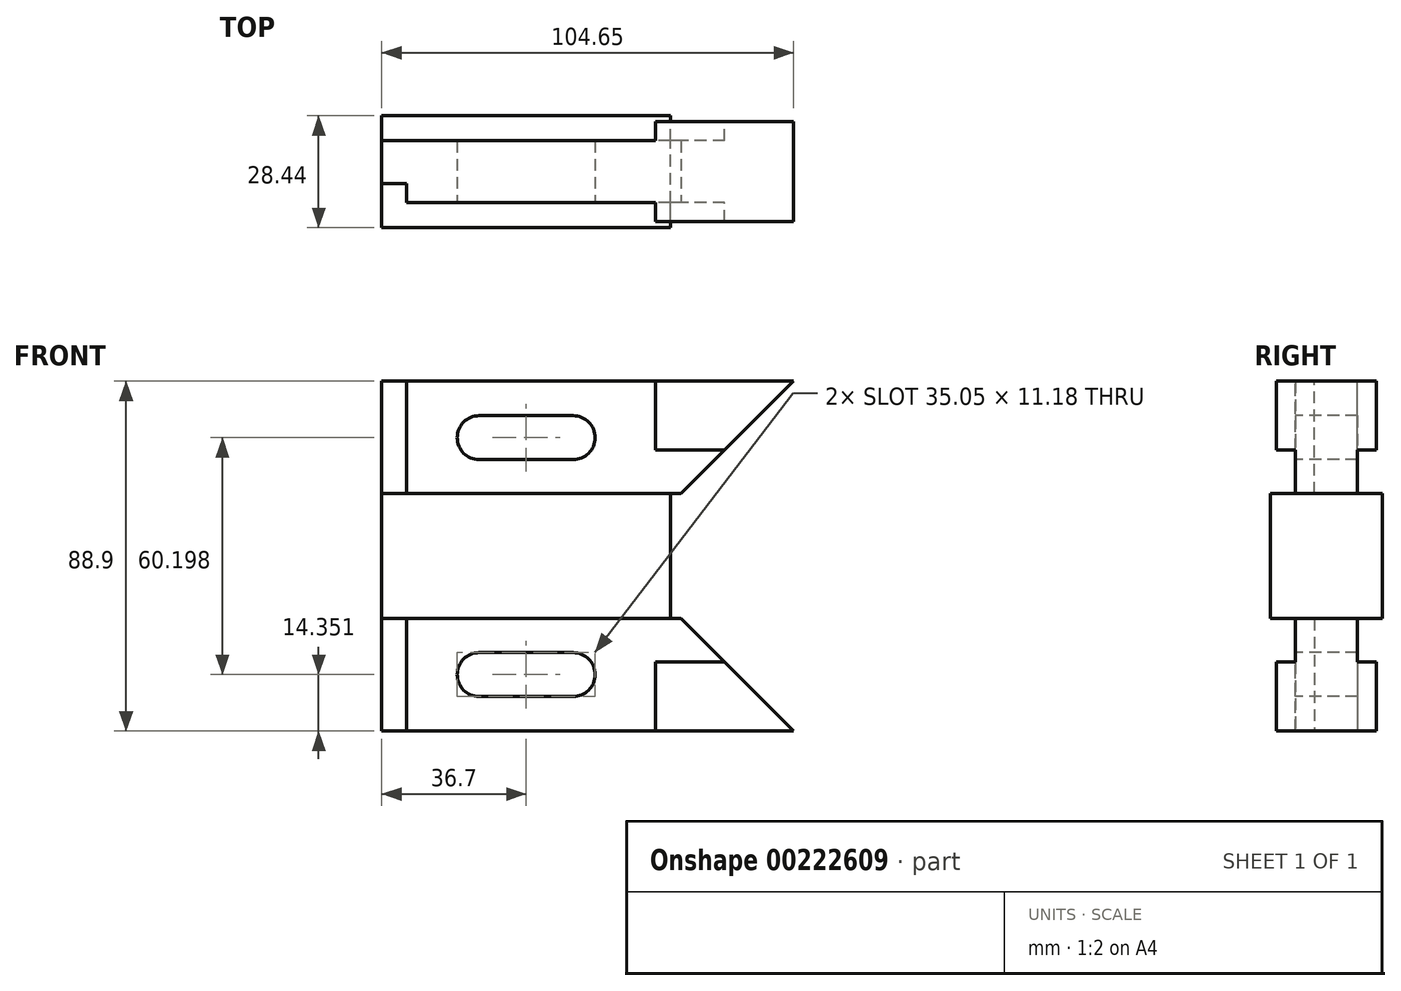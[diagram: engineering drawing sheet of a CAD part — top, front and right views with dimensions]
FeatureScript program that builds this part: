
annotation { "Feature Type Name" : "Feature", "Feature Type Description" : "" }
export const myFeature = defineFeature(function(context is Context, id is Id, definition is map)
    precondition{}
    {
        {
            var Q0;
            Q0=qCreatedBy(makeId("Front.planeOp"),FACE);
            var sketch = newSketch(context, id + "F0", { "sketchPlane" : qUnion([Q0])});
            skLineSegment(sketch, "E0.bottom", {"start": v(36.7, 15.88) * mm, "end": v(-36.7, 15.88) * mm});
            skLineSegment(sketch, "E0.top", {"start": v(36.7, -15.88) * mm, "end": v(-36.7, -15.88) * mm});
            skLineSegment(sketch, "E0.left", {"start": v(36.7, 15.88) * mm, "end": v(36.7, -15.87) * mm});
            skLineSegment(sketch, "E0.right", {"start": v(-36.7, 15.88) * mm, "end": v(-36.7, -15.88) * mm});
            skPoint(sketch, "E0.middle", {"position": v(0, 0) * mm});
            skLineSegment(sketch, "E1", {"start": v(-112.23, 0) * mm, "end": v(159.14, 0) * mm, "construction": true});
            skSolve(sketch);
        }
        {
            var Q0;
            Q0 = qSketchRegion(id + "F0", true);
            extrude(context, id + "F1", {"entities" : qUnion([Q0]), "endBound" : BoundingType.SYMMETRIC, "depth" : 28.45 * mm});
        }
        {
            var Q0;
            Q0=makeQuery(id+"F1.opExtrude","SWEPT_FACE",FACE,{"disambiguationData":[OSD([sQuery(id+"F0.wireOp",EDGE,"E0.right")])]});
            var sketch = newSketch(context, id + "F2", { "sketchPlane" : qUnion([Q0])});
            skLineSegment(sketch, "E2.0", {"start": v(14.22, 15.88) * mm, "end": v(-14.22, 15.88) * mm});
            skLineSegment(sketch, "E3.bottom", {"start": v(7.87, 15.88) * mm, "end": v(-7.87, 15.88) * mm});
            skLineSegment(sketch, "E3.top", {"start": v(7.87, 44.45) * mm, "end": v(-7.87, 44.45) * mm});
            skLineSegment(sketch, "E3.left", {"start": v(7.87, 15.88) * mm, "end": v(7.87, 44.45) * mm});
            skLineSegment(sketch, "E3.right", {"start": v(-7.87, 15.88) * mm, "end": v(-7.87, 44.45) * mm});
            skPoint(sketch, "E3.middle", {"position": v(0, 30.16) * mm});
            skPoint(sketch, "E3.middle.positionSnap0", {"position": v(0, 15.88) * mm});
            skPoint(sketch, "E3.centerSnap0", {"position": v(0, 15.88) * mm});
            skSolve(sketch);
        }
        {
            var Q0;
            Q0 = qSketchRegion(id + "F2", true);
            extrude(context, id + "F3", {"entities" : qUnion([Q0]), "operationType" : NewBodyOperationType.ADD, "oppositeDirection" : true, "depth" : 104.65 * mm});
        }
        {
            var Q0;
            Q0=makeQuery(id+"F3.opExtrude","SWEPT_FACE",FACE,{"disambiguationData":[OSD([sQuery(id+"F2.wireOp",EDGE,"E3.left")])]});
            var sketch = newSketch(context, id + "F4", { "sketchPlane" : qUnion([Q0])});
            skLineSegment(sketch, "E4", {"start": v(67.95, 44.45) * mm, "end": v(35.06, 11.57) * mm});
            skLineSegment(sketch, "E5", {"start": v(39.37, 15.87) * mm, "end": v(67.95, 15.87) * mm});
            skLineSegment(sketch, "E6", {"start": v(67.95, 15.87) * mm, "end": v(67.95, 44.45) * mm});
            skSolve(sketch);
        }
        {
            var Q0;
            Q0 = qSketchRegion(id + "F4", true);
            extrude(context, id + "F5", {"entities" : qUnion([Q0]), "operationType" : NewBodyOperationType.REMOVE, "endBound" : BoundingType.THROUGH_ALL, "oppositeDirection" : true, "depth" : 25.4 * mm});
        }
        {
            var Q0;
            Q0=qCreatedBy(makeId("Front.planeOp"),FACE);
            var sketch = newSketch(context, id + "F6", { "sketchPlane" : qUnion([Q0])});
            skLineSegment(sketch, "E7.0", {"start": v(67.95, 44.45) * mm, "end": v(-36.7, 44.45) * mm});
            skLineSegment(sketch, "E8.0", {"start": v(67.95, 44.45) * mm, "end": v(39.37, 15.87) * mm});
            skLineSegment(sketch, "E9", {"start": v(32.9, 44.45) * mm, "end": v(32.9, 26.92) * mm});
            skLineSegment(sketch, "E10", {"start": v(32.9, 26.92) * mm, "end": v(50.42, 26.92) * mm});
            skSolve(sketch);
        }
        {
            var Q0;
            Q0 = qSketchRegion(id + "F6", true);
            extrude(context, id + "F7", {"entities" : qUnion([Q0]), "operationType" : NewBodyOperationType.ADD, "endBound" : BoundingType.SYMMETRIC, "depth" : 25.4 * mm});
        }
        {
            var Q0;
            Q0=makeQuery(id+"F3.opExtrude","SWEPT_FACE",FACE,{"disambiguationData":[OSD([sQuery(id+"F2.wireOp",EDGE,"E3.left")])]});
            var sketch = newSketch(context, id + "F8", { "sketchPlane" : qUnion([Q0])});
            skLineSegment(sketch, "E11", {"start": v(-36.7, 44.45) * mm, "end": v(-30.35, 44.45) * mm});
            skLineSegment(sketch, "E12", {"start": v(-30.35, 44.45) * mm, "end": v(-30.35, 15.88) * mm});
            skLineSegment(sketch, "E13", {"start": v(-30.35, 15.88) * mm, "end": v(-36.7, 15.88) * mm});
            skLineSegment(sketch, "E14", {"start": v(-36.7, 15.88) * mm, "end": v(-36.7, 44.45) * mm});
            skSolve(sketch);
        }
        {
            var Q0;
            Q0 = qSketchRegion(id + "F8", true);
            extrude(context, id + "F9", {"entities" : qUnion([Q0]), "operationType" : NewBodyOperationType.REMOVE, "oppositeDirection" : true, "depth" : 4.83 * mm});
        }
        {
            var Q0;
            Q0=makeQuery(id+"F3.opExtrude","SWEPT_FACE",FACE,{"disambiguationData":[OSD([sQuery(id+"F2.wireOp",EDGE,"E3.left")])]});
            var sketch = newSketch(context, id + "F10", { "sketchPlane" : qUnion([Q0])});
            skLineSegment(sketch, "E15.bottom", {"start": v(11.94, 24.51) * mm, "end": v(-11.94, 24.51) * mm});
            skLineSegment(sketch, "E15.top", {"start": v(11.94, 35.69) * mm, "end": v(-11.94, 35.69) * mm});
            skPoint(sketch, "E15.middle", {"position": v(0, 30.1) * mm});
            skCircle(sketch, "E16", {"center": v(-11.94, 30.1) * mm, "radius": 5.59 * mm});
            skCircle(sketch, "E17", {"center": v(11.94, 30.1) * mm, "radius": 5.59 * mm});
            skPoint(sketch, "E18.orphan", {"position": v(-17.53, 35.69) * mm});
            skPoint(sketch, "E19.orphan", {"position": v(-17.53, 24.51) * mm});
            skPoint(sketch, "E20.orphan", {"position": v(17.53, 35.69) * mm});
            skPoint(sketch, "E21.orphan", {"position": v(17.53, 24.51) * mm});
            skSolve(sketch);
        }
        {
            var Q0;
            Q0 = qSketchRegion(id + "F10", true);
            extrude(context, id + "F11", {"entities" : qUnion([Q0]), "operationType" : NewBodyOperationType.REMOVE, "endBound" : BoundingType.THROUGH_ALL, "oppositeDirection" : true, "depth" : 25.4 * mm});
        }
        {
            var Q0;
            Q0=makeQuery(id+"F1.opExtrude","SWEPT_BODY",BODY,{"disambiguationData":[OSD([sQuery(id+"F0.wireOp",EDGE,"E0.bottom"),sQuery(id+"F0.wireOp",EDGE,"E0.top"),sQuery(id+"F0.wireOp",EDGE,"E0.left"),sQuery(id+"F0.wireOp",EDGE,"E0.right")])]});
            var Q1;
            Q1=qCreatedBy(makeId("Top.planeOp"),FACE);
            mirror(context, id + "F12", {"operationType" : NewBodyOperationType.ADD, "entities" : qUnion([Q0]), "mirrorPlane" : qUnion([Q1])});
        }
    });
